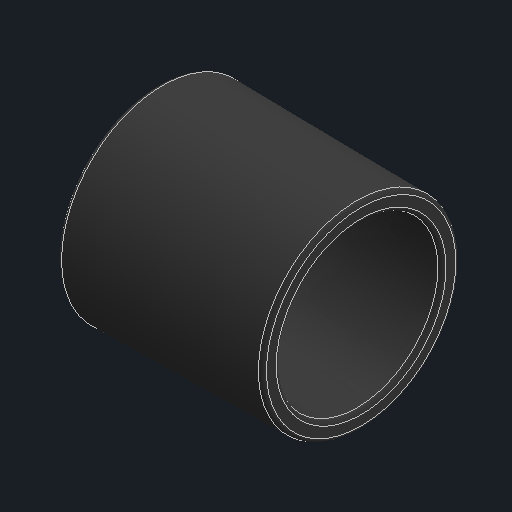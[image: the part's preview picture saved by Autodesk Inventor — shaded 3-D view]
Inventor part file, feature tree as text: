
AUTODESK INVENTOR PART (.ipt)
format: ipt  version: 2024.1 (Build 281209000, 209)  size: 214,016 bytes
history: native  units: mm
features: revolve x1, sketch x1
ambient origin geometry x8: Origin, YZ Plane, XZ Plane, XY Plane, X Axis, Y Axis, Z Axis, Center Point
bodies: Solid1 (feature_tree)
feature tree (2):
  revolve  "Revolution1"  [1 undecoded]
  sketch  "Sketch1"  dims[d0=13.0mm d1=11.0mm d2=5.0mm d3=1.1mm d5=2.0mm d6=6.25mm d7=60.0mm d8=0.5mm d9=0.25mm d10=90.0deg d11=0.872665mm]
note: 1 required parameter value undecoded (feature->parameter linkage not recoverable at this tier; creation-order binding heuristic only, values carry confidence <= 0.55)
